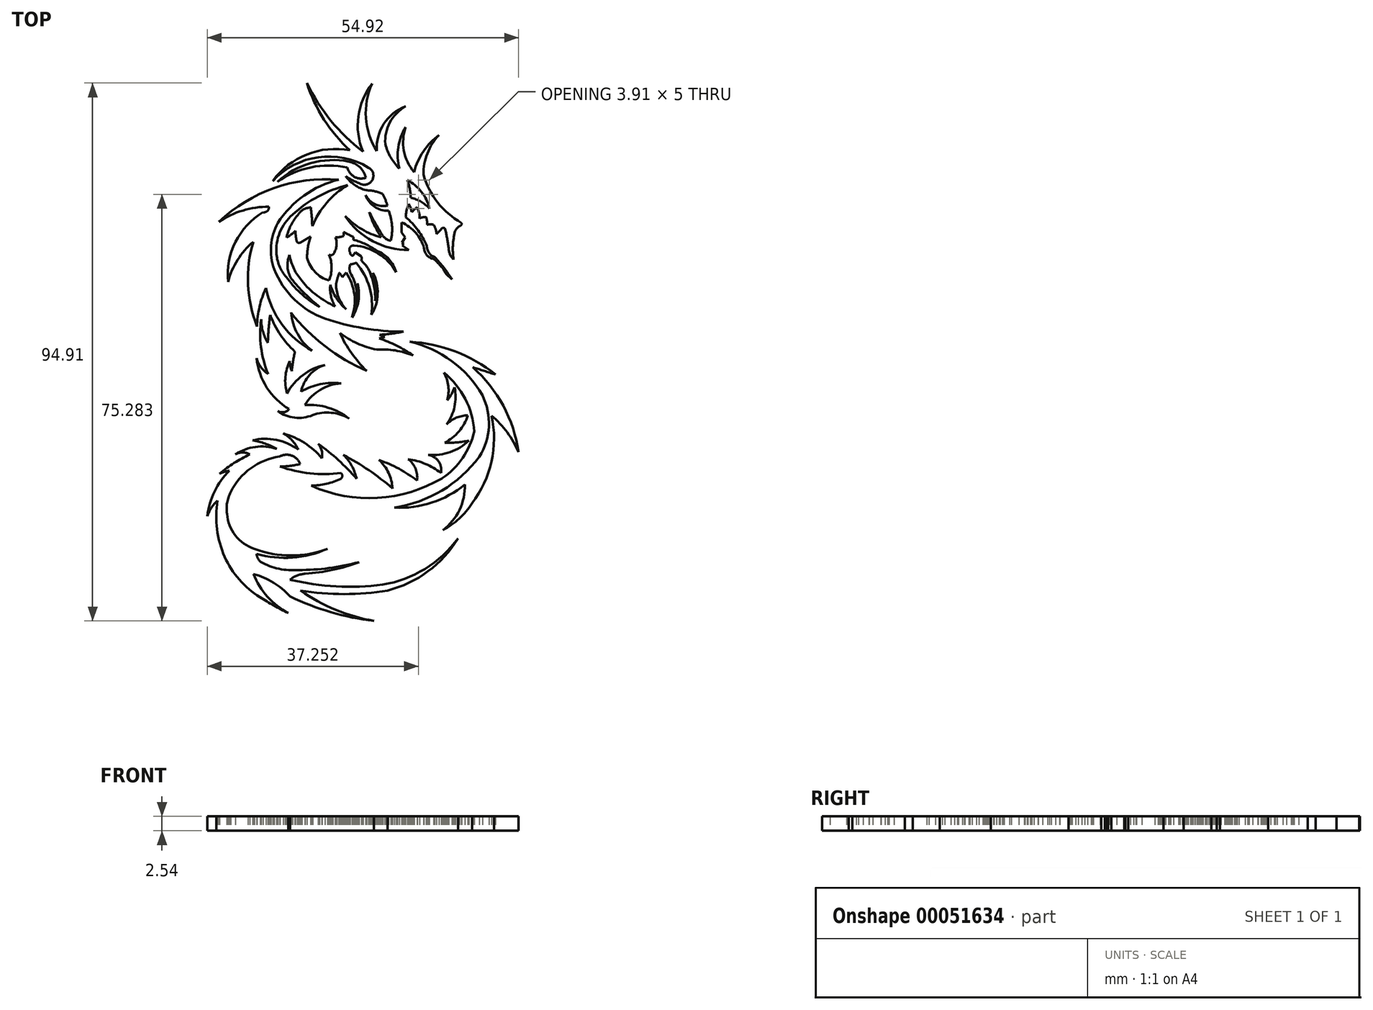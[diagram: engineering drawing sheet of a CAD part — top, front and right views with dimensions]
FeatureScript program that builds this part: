
annotation { "Feature Type Name" : "Feature", "Feature Type Description" : "" }
export const myFeature = defineFeature(function(context is Context, id is Id, definition is map)
    precondition{}
    {
        {
            var Q0;
            Q0=qCreatedBy(makeId("Top.planeOp"),FACE);
            var sketch = newSketch(context, id + "F0", { "sketchPlane" : qUnion([Q0])});
            skArc(sketch, "E0", {"start": v(-30.65, 39.22) * mm, "mid": v(-28.15, 34.33) * mm, "end": v(-23.98, 30.75) * mm});
            skArc(sketch, "E1", {"start": v(-27.91, 46.24) * mm, "mid": v(-29.97, 43) * mm, "end": v(-30.65, 39.22) * mm});
            skArc(sketch, "E2", {"start": v(-27.91, 46.24) * mm, "mid": v(-30.67, 43.35) * mm, "end": v(-32.32, 39.7) * mm});
            skArc(sketch, "E3", {"start": v(-33.8, 47.63) * mm, "mid": v(-34.11, 43.47) * mm, "end": v(-32.32, 39.7) * mm});
            skArc(sketch, "E4", {"start": v(-33.8, 47.63) * mm, "mid": v(-35.12, 44.08) * mm, "end": v(-34.92, 40.3) * mm});
            skArc(sketch, "E5", {"start": v(-37.4, 44.6) * mm, "mid": v(-36.44, 42.3) * mm, "end": v(-34.92, 40.3) * mm});
            skArc(sketch, "E6", {"start": v(-33.82, 51.28) * mm, "mid": v(-36.58, 48.47) * mm, "end": v(-37.4, 44.6) * mm});
            skArc(sketch, "E7", {"start": v(-33.82, 51.28) * mm, "mid": v(-37.67, 48.18) * mm, "end": v(-38.9, 43.4) * mm});
            skArc(sketch, "E8", {"start": v(-39.73, 55.3) * mm, "mid": v(-40.83, 49.25) * mm, "end": v(-38.9, 43.4) * mm});
            skArc(sketch, "E9", {"start": v(-39.73, 55.3) * mm, "mid": v(-42.15, 49.52) * mm, "end": v(-41.34, 43.3) * mm});
            skArc(sketch, "E10", {"start": v(-51.25, 55.4) * mm, "mid": v(-47, 48.77) * mm, "end": v(-41.34, 43.3) * mm});
            skArc(sketch, "E11", {"start": v(-51.25, 55.4) * mm, "mid": v(-48.2, 48.97) * mm, "end": v(-43.64, 43.52) * mm});
            skArc(sketch, "E12", {"start": v(-43.64, 43.52) * mm, "mid": v(-51.25, 42.81) * mm, "end": v(-57.28, 38.12) * mm});
            skArc(sketch, "E13", {"start": v(-40.35, 40.47) * mm, "mid": v(-49.23, 42.31) * mm, "end": v(-57.28, 38.12) * mm});
            skArc(sketch, "E14", {"start": v(-41.33, 37.48) * mm, "mid": v(-39.58, 38.56) * mm, "end": v(-40.35, 40.47) * mm});
            skArc(sketch, "E15", {"start": v(-44.38, 38.98) * mm, "mid": v(-42.91, 38.11) * mm, "end": v(-41.33, 37.48) * mm});
            skArc(sketch, "E16", {"start": v(-44.38, 38.98) * mm, "mid": v(-42.8, 37.4) * mm, "end": v(-40.77, 36.48) * mm});
            skArc(sketch, "E17", {"start": v(-37.91, 35.86) * mm, "mid": v(-39.31, 36.3) * mm, "end": v(-40.77, 36.48) * mm});
            skArc(sketch, "E18", {"start": v(-37.01, 33.75) * mm, "mid": v(-37.4, 34.83) * mm, "end": v(-37.91, 35.86) * mm});
            skArc(sketch, "E19", {"start": v(-40.85, 35.6) * mm, "mid": v(-39.24, 34.04) * mm, "end": v(-37.01, 33.75) * mm});
            skArc(sketch, "E20", {"start": v(-40.85, 35.6) * mm, "mid": v(-39.3, 33.56) * mm, "end": v(-36.83, 32.89) * mm});
            skArc(sketch, "E21", {"start": v(-44.1, 40.51) * mm, "mid": v(-50.54, 40.52) * mm, "end": v(-56.45, 37.97) * mm});
            skArc(sketch, "E22", {"start": v(-44.1, 40.51) * mm, "mid": v(-42.88, 38.87) * mm, "end": v(-40.83, 38.7) * mm});
            skArc(sketch, "E23", {"start": v(-40.83, 38.7) * mm, "mid": v(-41.92, 40.55) * mm, "end": v(-43.82, 41.54) * mm});
            skArc(sketch, "E24", {"start": v(-43.82, 41.54) * mm, "mid": v(-50.56, 41.26) * mm, "end": v(-56.45, 37.97) * mm});
            skArc(sketch, "E25", {"start": v(-36.45, 27.58) * mm, "mid": v(-36.2, 30.27) * mm, "end": v(-36.83, 32.89) * mm});
            skArc(sketch, "E26", {"start": v(-37.87, 28.52) * mm, "mid": v(-37.26, 27.9) * mm, "end": v(-36.45, 27.58) * mm});
            skArc(sketch, "E27", {"start": v(-40.23, 32.6) * mm, "mid": v(-39.08, 30.55) * mm, "end": v(-37.87, 28.52) * mm});
            skArc(sketch, "E28", {"start": v(-40.23, 32.6) * mm, "mid": v(-39.32, 30.32) * mm, "end": v(-38.12, 28.17) * mm});
            skArc(sketch, "E29", {"start": v(-44.48, 31.94) * mm, "mid": v(-41.56, 29.61) * mm, "end": v(-38.12, 28.17) * mm});
            skArc(sketch, "E30", {"start": v(-44.48, 31.94) * mm, "mid": v(-39.63, 27.52) * mm, "end": v(-33.25, 25.95) * mm});
            skLineSegment(sketch, "E31", {"start": v(-33.25, 25.95) * mm, "end": v(-34.39, 26.7) * mm});
            skLineSegment(sketch, "E32", {"start": v(-34.39, 26.7) * mm, "end": v(-34.17, 27.04) * mm});
            skLineSegment(sketch, "E33", {"start": v(-34.17, 27.04) * mm, "end": v(-34.49, 27.25) * mm});
            skLineSegment(sketch, "E34", {"start": v(-34.49, 27.25) * mm, "end": v(-33.88, 28.16) * mm});
            skLineSegment(sketch, "E35", {"start": v(-33.88, 28.16) * mm, "end": v(-34.5, 28.99) * mm});
            skLineSegment(sketch, "E36", {"start": v(-34.5, 28.99) * mm, "end": v(-34.5, 30.8) * mm});
            skArc(sketch, "E37", {"start": v(-30.56, 26.27) * mm, "mid": v(-32.03, 28.98) * mm, "end": v(-34.5, 30.8) * mm});
            skArc(sketch, "E38", {"start": v(-30.56, 26.27) * mm, "mid": v(-30.05, 25.03) * mm, "end": v(-28.88, 24.37) * mm});
            skArc(sketch, "E39", {"start": v(-26.66, 21.73) * mm, "mid": v(-27.64, 23.16) * mm, "end": v(-28.88, 24.37) * mm});
            skLineSegment(sketch, "E40", {"start": v(-26.66, 21.73) * mm, "end": v(-25.6, 20.73) * mm});
            skArc(sketch, "E41", {"start": v(-25.6, 20.73) * mm, "mid": v(-27.04, 22.77) * mm, "end": v(-28.66, 24.67) * mm});
            skArc(sketch, "E42", {"start": v(-30.06, 26.64) * mm, "mid": v(-29.68, 25.43) * mm, "end": v(-28.66, 24.67) * mm});
            skArc(sketch, "E43", {"start": v(-30.06, 26.64) * mm, "mid": v(-31.62, 29.41) * mm, "end": v(-33.8, 31.73) * mm});
            skArc(sketch, "E44", {"start": v(-33.24, 34.08) * mm, "mid": v(-33.64, 32.93) * mm, "end": v(-33.8, 31.73) * mm});
            skArc(sketch, "E45", {"start": v(-32.75, 32.61) * mm, "mid": v(-32.92, 33.37) * mm, "end": v(-33.24, 34.08) * mm});
            skArc(sketch, "E46", {"start": v(-31.8, 33.49) * mm, "mid": v(-32.29, 33.06) * mm, "end": v(-32.75, 32.61) * mm});
            skArc(sketch, "E47", {"start": v(-31.35, 31.52) * mm, "mid": v(-31.44, 32.54) * mm, "end": v(-31.8, 33.49) * mm});
            skArc(sketch, "E48", {"start": v(-30.2, 31.73) * mm, "mid": v(-30.8, 31.7) * mm, "end": v(-31.35, 31.52) * mm});
            skArc(sketch, "E49", {"start": v(-30.04, 30.38) * mm, "mid": v(-30.04, 31.07) * mm, "end": v(-30.2, 31.73) * mm});
            skArc(sketch, "E50", {"start": v(-28.88, 30.38) * mm, "mid": v(-29.46, 30.48) * mm, "end": v(-30.04, 30.38) * mm});
            skArc(sketch, "E51", {"start": v(-28.37, 28.76) * mm, "mid": v(-28.5, 29.61) * mm, "end": v(-28.88, 30.38) * mm});
            skArc(sketch, "E52", {"start": v(-28.37, 28.76) * mm, "mid": v(-27.87, 29.27) * mm, "end": v(-27.38, 29.8) * mm});
            skArc(sketch, "E53", {"start": v(-26.81, 29.56) * mm, "mid": v(-27.04, 29.83) * mm, "end": v(-27.38, 29.8) * mm});
            skArc(sketch, "E54", {"start": v(-26.23, 26.32) * mm, "mid": v(-26.48, 27.95) * mm, "end": v(-26.81, 29.56) * mm});
            skArc(sketch, "E55", {"start": v(-26.23, 26.32) * mm, "mid": v(-25.99, 25.22) * mm, "end": v(-25.35, 24.28) * mm});
            skArc(sketch, "E56", {"start": v(-25.1, 29.19) * mm, "mid": v(-25.46, 26.74) * mm, "end": v(-25.35, 24.28) * mm});
            skArc(sketch, "E57", {"start": v(-24.27, 30.17) * mm, "mid": v(-24.76, 29.74) * mm, "end": v(-25.1, 29.19) * mm});
            skArc(sketch, "E58", {"start": v(-24.27, 30.17) * mm, "mid": v(-23.97, 30.38) * mm, "end": v(-23.98, 30.75) * mm});
            skArc(sketch, "E59", {"start": v(-29.6, 33.27) * mm, "mid": v(-31.01, 36.2) * mm, "end": v(-33.51, 38.27) * mm});
            skArc(sketch, "E60", {"start": v(-29.6, 33.27) * mm, "mid": v(-31.1, 34.46) * mm, "end": v(-32.9, 35.15) * mm});
            skArc(sketch, "E61", {"start": v(-32.9, 35.15) * mm, "mid": v(-33.08, 36.73) * mm, "end": v(-33.51, 38.27) * mm});
            skArc(sketch, "E62", {"start": v(-44.07, 37.38) * mm, "mid": v(-49.23, 35.39) * mm, "end": v(-53.76, 32.2) * mm});
            skArc(sketch, "E63", {"start": v(-53.76, 32.2) * mm, "mid": v(-56.03, 29.04) * mm, "end": v(-56.6, 25.2) * mm});
            skArc(sketch, "E64", {"start": v(-56.6, 25.2) * mm, "mid": v(-55.99, 22.86) * mm, "end": v(-54.62, 20.88) * mm});
            skArc(sketch, "E65", {"start": v(-54.62, 20.88) * mm, "mid": v(-52.08, 18.07) * mm, "end": v(-48.97, 15.88) * mm});
            skArc(sketch, "E66", {"start": v(-54, 20.88) * mm, "mid": v(-51.62, 18.24) * mm, "end": v(-48.97, 15.88) * mm});
            skArc(sketch, "E67", {"start": v(-54.31, 25.05) * mm, "mid": v(-54.65, 22.93) * mm, "end": v(-54, 20.88) * mm});
            skArc(sketch, "E68", {"start": v(-54.31, 25.05) * mm, "mid": v(-53.52, 22.62) * mm, "end": v(-52.11, 20.49) * mm});
            skArc(sketch, "E69", {"start": v(-52.11, 20.49) * mm, "mid": v(-49.47, 17.9) * mm, "end": v(-46.27, 16.02) * mm});
            skArc(sketch, "E70", {"start": v(-47.1, 19.82) * mm, "mid": v(-47, 17.85) * mm, "end": v(-46.27, 16.02) * mm});
            skArc(sketch, "E71", {"start": v(-47.1, 19.82) * mm, "mid": v(-46.04, 17.46) * mm, "end": v(-44.33, 15.5) * mm});
            skArc(sketch, "E72", {"start": v(-46.1, 19.91) * mm, "mid": v(-45.63, 17.54) * mm, "end": v(-44.33, 15.5) * mm});
            skArc(sketch, "E73", {"start": v(-45.5, 21.93) * mm, "mid": v(-45.84, 20.93) * mm, "end": v(-46.1, 19.91) * mm});
            skArc(sketch, "E74", {"start": v(-44.98, 21.14) * mm, "mid": v(-45.23, 21.55) * mm, "end": v(-45.5, 21.93) * mm});
            skArc(sketch, "E75", {"start": v(-44.98, 21.14) * mm, "mid": v(-44.66, 21.54) * mm, "end": v(-44.33, 21.95) * mm});
            skArc(sketch, "E76", {"start": v(-43.3, 14) * mm, "mid": v(-42.86, 18.1) * mm, "end": v(-44.33, 21.95) * mm});
            skArc(sketch, "E77", {"start": v(-43.3, 14) * mm, "mid": v(-42.16, 16.91) * mm, "end": v(-42.28, 20.03) * mm});
            skArc(sketch, "E78", {"start": v(-42.64, 15.93) * mm, "mid": v(-42.28, 17.96) * mm, "end": v(-42.28, 20.03) * mm});
            skArc(sketch, "E79", {"start": v(-42.64, 15.93) * mm, "mid": v(-42.54, 19.02) * mm, "end": v(-43.58, 21.94) * mm});
            skArc(sketch, "E80", {"start": v(-43.58, 23.4) * mm, "mid": v(-43.71, 22.67) * mm, "end": v(-43.58, 21.94) * mm});
            skArc(sketch, "E81", {"start": v(-43.58, 23.4) * mm, "mid": v(-43.03, 23.5) * mm, "end": v(-42.5, 23.67) * mm});
            skArc(sketch, "E82", {"start": v(-39.85, 14.5) * mm, "mid": v(-40.19, 19.38) * mm, "end": v(-42.5, 23.67) * mm});
            skArc(sketch, "E83", {"start": v(-39.85, 14.5) * mm, "mid": v(-38.74, 18.16) * mm, "end": v(-39.58, 21.89) * mm});
            skArc(sketch, "E84", {"start": v(-39.2, 16.94) * mm, "mid": v(-39.09, 19.44) * mm, "end": v(-39.58, 21.89) * mm});
            skArc(sketch, "E85", {"start": v(-39.2, 16.94) * mm, "mid": v(-39.33, 19.35) * mm, "end": v(-40, 21.67) * mm});
            skArc(sketch, "E86", {"start": v(-40, 21.67) * mm, "mid": v(-40.65, 22.99) * mm, "end": v(-41.64, 24.08) * mm});
            skArc(sketch, "E87", {"start": v(-41.64, 24.08) * mm, "mid": v(-41.58, 24.45) * mm, "end": v(-41.64, 24.8) * mm});
            skLineSegment(sketch, "E88", {"start": v(-41.64, 24.8) * mm, "end": v(-42.69, 25.54) * mm});
            skLineSegment(sketch, "E89", {"start": v(-42.69, 25.54) * mm, "end": v(-43.1, 24.95) * mm});
            skArc(sketch, "E90", {"start": v(-43.61, 25.52) * mm, "mid": v(-43.5, 25.12) * mm, "end": v(-43.1, 24.95) * mm});
            skArc(sketch, "E91", {"start": v(-42.9, 26.75) * mm, "mid": v(-43.65, 26.36) * mm, "end": v(-43.61, 25.52) * mm});
            skArc(sketch, "E92", {"start": v(-35.5, 22.06) * mm, "mid": v(-38.63, 25.3) * mm, "end": v(-42.9, 26.75) * mm});
            skArc(sketch, "E93", {"start": v(-35.5, 22.06) * mm, "mid": v(-36.74, 24.3) * mm, "end": v(-38.86, 25.77) * mm});
            skArc(sketch, "E94", {"start": v(-38.86, 25.77) * mm, "mid": v(-40.86, 26.95) * mm, "end": v(-43.04, 27.76) * mm});
            skArc(sketch, "E95", {"start": v(-43.04, 27.76) * mm, "mid": v(-43.03, 28) * mm, "end": v(-43.04, 28.23) * mm});
            skArc(sketch, "E96", {"start": v(-43.04, 28.23) * mm, "mid": v(-43.9, 28.67) * mm, "end": v(-44.76, 29.1) * mm});
            skArc(sketch, "E97", {"start": v(-44.76, 28.4) * mm, "mid": v(-44.72, 28.75) * mm, "end": v(-44.76, 29.1) * mm});
            skArc(sketch, "E98", {"start": v(-46.2, 28.17) * mm, "mid": v(-45.47, 28.22) * mm, "end": v(-44.76, 28.4) * mm});
            skArc(sketch, "E99", {"start": v(-46.66, 25.12) * mm, "mid": v(-46.02, 26.58) * mm, "end": v(-46.2, 28.17) * mm});
            skArc(sketch, "E100", {"start": v(-47.34, 25.12) * mm, "mid": v(-47, 25.03) * mm, "end": v(-46.66, 25.12) * mm});
            skArc(sketch, "E101", {"start": v(-47.34, 20.54) * mm, "mid": v(-46.88, 22.83) * mm, "end": v(-47.34, 25.12) * mm});
            skArc(sketch, "E102", {"start": v(-51.2, 24.57) * mm, "mid": v(-49.8, 22.05) * mm, "end": v(-47.34, 20.54) * mm});
            skArc(sketch, "E103", {"start": v(-50.58, 28.31) * mm, "mid": v(-51.06, 26.47) * mm, "end": v(-51.2, 24.57) * mm});
            skArc(sketch, "E104", {"start": v(-50.58, 28.31) * mm, "mid": v(-51.46, 27.83) * mm, "end": v(-52.3, 27.29) * mm});
            skArc(sketch, "E105", {"start": v(-52.97, 27.29) * mm, "mid": v(-52.63, 27.2) * mm, "end": v(-52.3, 27.29) * mm});
            skArc(sketch, "E106", {"start": v(-53.23, 29.34) * mm, "mid": v(-53.2, 28.3) * mm, "end": v(-52.97, 27.29) * mm});
            skArc(sketch, "E107", {"start": v(-54.86, 28.12) * mm, "mid": v(-54.01, 28.68) * mm, "end": v(-53.23, 29.34) * mm});
            skArc(sketch, "E108", {"start": v(-52.71, 32.3) * mm, "mid": v(-54.04, 30.34) * mm, "end": v(-54.86, 28.12) * mm});
            skArc(sketch, "E109", {"start": v(-50.55, 33.43) * mm, "mid": v(-51.77, 33.13) * mm, "end": v(-52.71, 32.3) * mm});
            skArc(sketch, "E110", {"start": v(-50.3, 30.15) * mm, "mid": v(-50.38, 31.8) * mm, "end": v(-50.55, 33.43) * mm});
            skArc(sketch, "E111", {"start": v(-44.07, 37.38) * mm, "mid": v(-47.76, 34.26) * mm, "end": v(-50.3, 30.15) * mm});
            skArc(sketch, "E112", {"start": v(-45.67, 38.36) * mm, "mid": v(-57, 36.87) * mm, "end": v(-66.77, 30.92) * mm});
            skArc(sketch, "E113", {"start": v(-57.94, 33.58) * mm, "mid": v(-62.55, 32.91) * mm, "end": v(-66.77, 30.92) * mm});
            skArc(sketch, "E114", {"start": v(-58.97, 32.6) * mm, "mid": v(-58.21, 32.83) * mm, "end": v(-57.94, 33.58) * mm});
            skArc(sketch, "E115", {"start": v(-58.97, 32.6) * mm, "mid": v(-63.84, 27.36) * mm, "end": v(-65.15, 20.33) * mm});
            skArc(sketch, "E116", {"start": v(-60.7, 27.37) * mm, "mid": v(-63.48, 24.2) * mm, "end": v(-65.15, 20.33) * mm});
            skArc(sketch, "E117", {"start": v(-60.7, 27.37) * mm, "mid": v(-61.63, 19.86) * mm, "end": v(-60.06, 12.47) * mm});
            skArc(sketch, "E118", {"start": v(-58.46, 19.2) * mm, "mid": v(-59.6, 15.92) * mm, "end": v(-60.06, 12.47) * mm});
            skArc(sketch, "E119", {"start": v(-58.46, 19.2) * mm, "mid": v(-55.63, 12.78) * mm, "end": v(-50.33, 8.17) * mm});
            skArc(sketch, "E120", {"start": v(-54.03, 14.88) * mm, "mid": v(-52.9, 11.13) * mm, "end": v(-50.33, 8.17) * mm});
            skArc(sketch, "E121", {"start": v(-54.03, 14.88) * mm, "mid": v(-47.99, 8.91) * mm, "end": v(-40.67, 4.6) * mm});
            skArc(sketch, "E122", {"start": v(-45.41, 11.31) * mm, "mid": v(-43.35, 7.73) * mm, "end": v(-40.67, 4.6) * mm});
            skArc(sketch, "E123", {"start": v(-45.41, 11.31) * mm, "mid": v(-42.34, 9.47) * mm, "end": v(-38.93, 8.37) * mm});
            skArc(sketch, "E124", {"start": v(-32.51, 7.36) * mm, "mid": v(-35.67, 8.22) * mm, "end": v(-38.93, 8.37) * mm});
            skArc(sketch, "E125", {"start": v(-32.51, 7.36) * mm, "mid": v(-35.4, 9.06) * mm, "end": v(-38.47, 10.37) * mm});
            skLineSegment(sketch, "E126", {"start": v(-38.47, 10.37) * mm, "end": v(-37.48, 10.6) * mm});
            skLineSegment(sketch, "E127", {"start": v(-37.48, 10.6) * mm, "end": v(-38.38, 11) * mm});
            skArc(sketch, "E128", {"start": v(-38.38, 11) * mm, "mid": v(-36.3, 11.18) * mm, "end": v(-34.23, 11.53) * mm});
            skArc(sketch, "E129", {"start": v(-48.05, 13.84) * mm, "mid": v(-41.23, 12.13) * mm, "end": v(-34.23, 11.53) * mm});
            skArc(sketch, "E130", {"start": v(-57, 22.54) * mm, "mid": v(-53.46, 17.23) * mm, "end": v(-48.05, 13.84) * mm});
            skArc(sketch, "E131", {"start": v(-56.38, 30.7) * mm, "mid": v(-57.55, 26.69) * mm, "end": v(-57, 22.54) * mm});
            skArc(sketch, "E132", {"start": v(-45.67, 38.36) * mm, "mid": v(-51.74, 35.54) * mm, "end": v(-56.38, 30.7) * mm});
            skArc(sketch, "E133", {"start": v(-17.96, 3.97) * mm, "mid": v(-25.06, 8.04) * mm, "end": v(-33.07, 9.75) * mm});
            skArc(sketch, "E134", {"start": v(-17.96, 3.97) * mm, "mid": v(-19.96, 4.61) * mm, "end": v(-21.97, 5.23) * mm});
            skArc(sketch, "E135", {"start": v(-20.26, 0.3) * mm, "mid": v(-25.68, 6.35) * mm, "end": v(-33.07, 9.75) * mm});
            skArc(sketch, "E136", {"start": v(-20.8, -10.55) * mm, "mid": v(-19.11, -5.2) * mm, "end": v(-20.26, 0.3) * mm});
            skArc(sketch, "E137", {"start": v(-35.76, -19.51) * mm, "mid": v(-27.4, -16.51) * mm, "end": v(-20.8, -10.55) * mm});
            skArc(sketch, "E138", {"start": v(-35.76, -19.51) * mm, "mid": v(-29.16, -18.64) * mm, "end": v(-23.34, -15.42) * mm});
            skArc(sketch, "E139", {"start": v(-27.24, -23.5) * mm, "mid": v(-24.3, -19.93) * mm, "end": v(-23.34, -15.42) * mm});
            skArc(sketch, "E140", {"start": v(-27.24, -23.5) * mm, "mid": v(-24.36, -21.45) * mm, "end": v(-22.08, -18.75) * mm});
            skArc(sketch, "E141", {"start": v(-22.08, -18.75) * mm, "mid": v(-18.67, -11.4) * mm, "end": v(-18.62, -3.3) * mm});
            skArc(sketch, "E142", {"start": v(-13.89, -9.75) * mm, "mid": v(-15.88, -6.25) * mm, "end": v(-18.62, -3.3) * mm});
            skArc(sketch, "E143", {"start": v(-13.89, -9.75) * mm, "mid": v(-16.57, -1.53) * mm, "end": v(-21.97, 5.23) * mm});
            skArc(sketch, "E144", {"start": v(-21.7, -6.08) * mm, "mid": v(-23.29, -0.33) * mm, "end": v(-27.05, 4.3) * mm});
            skArc(sketch, "E145", {"start": v(-27.38, -14.33) * mm, "mid": v(-23.73, -10.76) * mm, "end": v(-21.7, -6.08) * mm});
            skArc(sketch, "E146", {"start": v(-50.47, -15.66) * mm, "mid": v(-38.76, -17.81) * mm, "end": v(-27.38, -14.33) * mm});
            skArc(sketch, "E147", {"start": v(-50.47, -15.66) * mm, "mid": v(-47.78, -15.3) * mm, "end": v(-45.2, -14.43) * mm});
            skArc(sketch, "E148", {"start": v(-45.2, -14.43) * mm, "mid": v(-45, -13.92) * mm, "end": v(-45.2, -13.42) * mm});
            skArc(sketch, "E149", {"start": v(-56.02, -12.25) * mm, "mid": v(-50.68, -13.48) * mm, "end": v(-45.2, -13.42) * mm});
            skArc(sketch, "E150", {"start": v(-56.02, -12.25) * mm, "mid": v(-54.2, -12.16) * mm, "end": v(-52.43, -11.8) * mm});
            skArc(sketch, "E151", {"start": v(-52.43, -11.8) * mm, "mid": v(-53.94, -10.34) * mm, "end": v(-56.04, -10.5) * mm});
            skArc(sketch, "E152", {"start": v(-56.04, -10.5) * mm, "mid": v(-61.13, -12.57) * mm, "end": v(-64.67, -16.8) * mm});
            skArc(sketch, "E153", {"start": v(-64.93, -13.02) * mm, "mid": v(-65.8, -13.2) * mm, "end": v(-66.63, -13.52) * mm});
            skArc(sketch, "E154", {"start": v(-61.33, -10.13) * mm, "mid": v(-64.09, -11.66) * mm, "end": v(-66.63, -13.52) * mm});
            skArc(sketch, "E155", {"start": v(-61.33, -10.13) * mm, "mid": v(-62.6, -9.8) * mm, "end": v(-63.86, -10.13) * mm});
            skArc(sketch, "E156", {"start": v(-56.58, -9.13) * mm, "mid": v(-60.33, -8.82) * mm, "end": v(-63.86, -10.13) * mm});
            skArc(sketch, "E157", {"start": v(-56.58, -9.13) * mm, "mid": v(-58.64, -8.21) * mm, "end": v(-60.84, -7.65) * mm});
            skArc(sketch, "E158", {"start": v(-52.77, -9.26) * mm, "mid": v(-56.63, -7.57) * mm, "end": v(-60.84, -7.65) * mm});
            skArc(sketch, "E159", {"start": v(-52.77, -9.26) * mm, "mid": v(-53.86, -7.63) * mm, "end": v(-55.42, -6.45) * mm});
            skArc(sketch, "E160", {"start": v(-48.6, -10.83) * mm, "mid": v(-51.66, -8.1) * mm, "end": v(-55.42, -6.45) * mm});
            skArc(sketch, "E161", {"start": v(-48.6, -10.83) * mm, "mid": v(-48.62, -9.47) * mm, "end": v(-49.25, -8.26) * mm});
            skArc(sketch, "E162", {"start": v(-42.47, -14.43) * mm, "mid": v(-45.68, -11.15) * mm, "end": v(-49.25, -8.26) * mm});
            skArc(sketch, "E163", {"start": v(-42.47, -14.43) * mm, "mid": v(-43.32, -12.15) * mm, "end": v(-44.78, -10.2) * mm});
            skArc(sketch, "E164", {"start": v(-36.14, -16.12) * mm, "mid": v(-40.3, -12.92) * mm, "end": v(-44.78, -10.2) * mm});
            skArc(sketch, "E165", {"start": v(-36.14, -16.12) * mm, "mid": v(-36.82, -13.4) * mm, "end": v(-38.5, -11.15) * mm});
            skArc(sketch, "E166", {"start": v(-31.8, -14.75) * mm, "mid": v(-35, -12.67) * mm, "end": v(-38.5, -11.15) * mm});
            skArc(sketch, "E167", {"start": v(-31.8, -14.75) * mm, "mid": v(-32.07, -12.65) * mm, "end": v(-33.36, -10.98) * mm});
            skArc(sketch, "E168", {"start": v(-27.57, -13.42) * mm, "mid": v(-30.3, -11.81) * mm, "end": v(-33.36, -10.98) * mm});
            skArc(sketch, "E169", {"start": v(-27.57, -13.42) * mm, "mid": v(-28, -11.34) * mm, "end": v(-29.8, -10.23) * mm});
            skArc(sketch, "E170", {"start": v(-26.9, -8.08) * mm, "mid": v(-24.76, -8.02) * mm, "end": v(-22.64, -7.7) * mm});
            skArc(sketch, "E171", {"start": v(-26.9, -8.08) * mm, "mid": v(-24.38, -6.06) * mm, "end": v(-22.81, -3.23) * mm});
            skArc(sketch, "E172", {"start": v(-22.81, -3.23) * mm, "mid": v(-24.84, -3.66) * mm, "end": v(-26.58, -4.8) * mm});
            skArc(sketch, "E173", {"start": v(-29.8, -10.23) * mm, "mid": v(-25.95, -9.73) * mm, "end": v(-22.64, -7.7) * mm});
            skArc(sketch, "E174", {"start": v(-26.58, -4.8) * mm, "mid": v(-25.17, -1.7) * mm, "end": v(-25.17, 1.7) * mm});
            skArc(sketch, "E175", {"start": v(-26.45, -0.58) * mm, "mid": v(-25.71, 0.5) * mm, "end": v(-25.17, 1.7) * mm});
            skArc(sketch, "E176", {"start": v(-26.45, -0.58) * mm, "mid": v(-26.27, 1.92) * mm, "end": v(-27.05, 4.3) * mm});
            skArc(sketch, "E177", {"start": v(-57.73, 14.46) * mm, "mid": v(-55.92, 10.98) * mm, "end": v(-53.36, 8) * mm});
            skArc(sketch, "E178", {"start": v(-53.36, 8) * mm, "mid": v(-53.68, 6.3) * mm, "end": v(-53.92, 4.56) * mm});
            skArc(sketch, "E179", {"start": v(-54.26, 6.36) * mm, "mid": v(-54.17, 5.45) * mm, "end": v(-53.92, 4.56) * mm});
            skArc(sketch, "E180", {"start": v(-54.26, 6.36) * mm, "mid": v(-55.04, 3.55) * mm, "end": v(-54.77, 0.65) * mm});
            skArc(sketch, "E181", {"start": v(-57.73, 14.46) * mm, "mid": v(-58, 12.01) * mm, "end": v(-58.13, 9.56) * mm});
            skArc(sketch, "E182", {"start": v(-59.31, 13.7) * mm, "mid": v(-59, 11.55) * mm, "end": v(-58.13, 9.56) * mm});
            skArc(sketch, "E183", {"start": v(-59.31, 13.7) * mm, "mid": v(-59.34, 8.8) * mm, "end": v(-58.1, 4.06) * mm});
            skArc(sketch, "E184", {"start": v(-60.11, 6.84) * mm, "mid": v(-59.35, 5.27) * mm, "end": v(-58.1, 4.06) * mm});
            skArc(sketch, "E185", {"start": v(-60.11, 6.84) * mm, "mid": v(-58.3, 1.67) * mm, "end": v(-54.37, -2.13) * mm});
            skArc(sketch, "E186", {"start": v(-56.39, -2.48) * mm, "mid": v(-55.31, -2.69) * mm, "end": v(-54.37, -2.13) * mm});
            skArc(sketch, "E187", {"start": v(-56.39, -2.48) * mm, "mid": v(-53.4, -3.64) * mm, "end": v(-50.23, -3.2) * mm});
            skArc(sketch, "E188", {"start": v(-43.8, -3.8) * mm, "mid": v(-46.94, -2.78) * mm, "end": v(-50.23, -3.2) * mm});
            skArc(sketch, "E189", {"start": v(-43.8, -3.8) * mm, "mid": v(-47.47, -1.89) * mm, "end": v(-51.58, -1.4) * mm});
            skArc(sketch, "E190", {"start": v(-45.22, 2.4) * mm, "mid": v(-48.87, 1.28) * mm, "end": v(-51.58, -1.4) * mm});
            skArc(sketch, "E191", {"start": v(-45.22, 2.4) * mm, "mid": v(-48.85, 2.26) * mm, "end": v(-52.25, 0.97) * mm});
            skArc(sketch, "E192", {"start": v(-48.04, 5.67) * mm, "mid": v(-50.78, 3.89) * mm, "end": v(-52.25, 0.97) * mm});
            skArc(sketch, "E193", {"start": v(-48.04, 5.67) * mm, "mid": v(-51.93, 3.88) * mm, "end": v(-54.77, 0.65) * mm});
            skArc(sketch, "E194", {"start": v(-64.93, -13.02) * mm, "mid": v(-67.55, -16.69) * mm, "end": v(-68.81, -21) * mm});
            skArc(sketch, "E195", {"start": v(-67, -18.3) * mm, "mid": v(-68.09, -19.53) * mm, "end": v(-68.81, -21) * mm});
            skArc(sketch, "E196", {"start": v(-67, -18.3) * mm, "mid": v(-67.1, -23.34) * mm, "end": v(-65.75, -28.2) * mm});
            skArc(sketch, "E197", {"start": v(-65.75, -28.2) * mm, "mid": v(-63.17, -32.24) * mm, "end": v(-59.52, -35.34) * mm});
            skArc(sketch, "E198", {"start": v(-59.52, -35.34) * mm, "mid": v(-57.05, -36.8) * mm, "end": v(-54.52, -38.12) * mm});
            skArc(sketch, "E199", {"start": v(-60.67, -31.23) * mm, "mid": v(-58.2, -35.23) * mm, "end": v(-54.52, -38.12) * mm});
            skArc(sketch, "E200", {"start": v(-54.2, -35.2) * mm, "mid": v(-57.15, -32.75) * mm, "end": v(-60.67, -31.23) * mm});
            skArc(sketch, "E201", {"start": v(-54.2, -35.2) * mm, "mid": v(-47, -37.98) * mm, "end": v(-39.42, -39.51) * mm});
            skArc(sketch, "E202", {"start": v(-52.36, -34.16) * mm, "mid": v(-46.18, -37.54) * mm, "end": v(-39.42, -39.51) * mm});
            skArc(sketch, "E203", {"start": v(-52.36, -34.16) * mm, "mid": v(-44.67, -34.79) * mm, "end": v(-36.98, -34.16) * mm});
            skArc(sketch, "E204", {"start": v(-36.98, -34.16) * mm, "mid": v(-29.87, -30.77) * mm, "end": v(-24.56, -24.94) * mm});
            skArc(sketch, "E205", {"start": v(-37.85, -33.11) * mm, "mid": v(-30.4, -30.33) * mm, "end": v(-24.56, -24.94) * mm});
            skArc(sketch, "E206", {"start": v(-54.2, -32.24) * mm, "mid": v(-46.07, -33.43) * mm, "end": v(-37.85, -33.11) * mm});
            skArc(sketch, "E207", {"start": v(-51.52, -31.2) * mm, "mid": v(-52.95, -31.5) * mm, "end": v(-54.2, -32.24) * mm});
            skArc(sketch, "E208", {"start": v(-51.52, -31.2) * mm, "mid": v(-46.7, -30.52) * mm, "end": v(-42.03, -29.15) * mm});
            skArc(sketch, "E209", {"start": v(-52.7, -30.54) * mm, "mid": v(-47.32, -30.2) * mm, "end": v(-42.03, -29.15) * mm});
            skArc(sketch, "E210", {"start": v(-59.42, -29.11) * mm, "mid": v(-56.17, -30.31) * mm, "end": v(-52.7, -30.54) * mm});
            skArc(sketch, "E211", {"start": v(-60.12, -27.72) * mm, "mid": v(-59.89, -28.48) * mm, "end": v(-59.42, -29.11) * mm});
            skArc(sketch, "E212", {"start": v(-60.12, -27.72) * mm, "mid": v(-53.77, -28.33) * mm, "end": v(-47.6, -26.78) * mm});
            skArc(sketch, "E213", {"start": v(-60.5, -26.78) * mm, "mid": v(-54.05, -27.97) * mm, "end": v(-47.6, -26.78) * mm});
            skArc(sketch, "E214", {"start": v(-65.33, -20.62) * mm, "mid": v(-63.86, -24.44) * mm, "end": v(-60.5, -26.78) * mm});
            skArc(sketch, "E215", {"start": v(-64.67, -16.8) * mm, "mid": v(-65.32, -18.65) * mm, "end": v(-65.33, -20.62) * mm});
            skSolve(sketch);
        }
        {
            var Q0;
            Q0 = qSketchRegion(id + "F0", true);
            extrude(context, id + "F1", {"entities" : qUnion([Q0]), "depth" : 2.54 * mm});
        }
    });
